# Revit family: 01-70-035-DN40-80
name_source: partatom
category: Pipe Accessories
units: mm (PartAtom-declared; Revit-internal decimal feet)

## family parameters
Always vertical = No
Cut with Voids When Loaded = No
Part Type = Valve - Breaks Into
Round Connector Dimension = Use Diameter
Shared = No
Work Plane-Based = No

## types (4) — shared parameters
Body_Wallthickness = 10 mm  [stored 0.0328084 ft]
Body_Wallthickness_1 = 20 mm  [stored 0.0656168 ft]
Body_Wallthickness_2 = 5 mm  [stored 0.0164042 ft]
Bonnet_Flange_cut = 8 mm  [stored 0.0262467 ft]
Bonnet_Flange_thickness = 15 mm  [stored 0.0492126 ft]
D = 63 mm
D1 = 10 mm  [stored 0.0328084 ft]
DN040_PN16 = 01-050-70-016
DN050_PN16 = 01-063-70-016
DN065_PN16 = 01-075-70-016
DN080_PN16 = 01-090-70-0146499
Description_ = AVK GATE VALVE, SUPA PLUS™
Fillet_Thickness = 6 mm  [stored 0.019685 ft]
Flange_Thickness = 19 mm  [stored 0.062336 ft]
Flange_width = 30 mm  [stored 0.0984252 ft]
Ftc = 4 mm  [stored 0.0131234 ft]
L1 = 229 mm
Name_Height_reference = 10 mm  [stored 0.0328084 ft]
R2f = 15 mm  [stored 0.0492126 ft]
Rib_Height_Reference_1 = 120 mm
Rib_Height_Reference_2 = 110 mm
Rib_Height_Reference_3 = 100 mm
Rib_Thickness = 18 mm  [stored 0.0590551 ft]
Search_table = 01-70-035-DN40-80
URL product pages = https://www.avkvalves.com
zero-valued in all types: Bottom_Reference

## per-type parameters (varying)
- DN040_PN16: At=46 mm  [stored 0.150919 ft]; Body_Height=101 mm; Body_depth=92 mm; Body_width=74 mm; Bonnet_Flange_Depth=118 mm; Bonnet_Flange_Width=68 mm; Bonnet_Height=38 mm; Bonnet_Reference_height=91 mm; Bonnet_Thickness=75 mm; Bt=75 mm; Bt_2=68 mm; CL _Thickness=26 mm; CL_Height=51 mm; Cut_Reference=624 mm; D2=29 mm  [stored 0.0951444 ft]; Dd=50 mm; Dd_ref=45 mm  [stored 0.147638 ft]; Dd_ref_1=25 mm  [stored 0.082021 ft]; E=14 mm  [stored 0.0459318 ft]; F=7 mm  [stored 0.0229659 ft]; F1=17 mm  [stored 0.0557743 ft]; Flange_OR=75 mm; Flange_Thickness_cut=28 mm; Flange_depth=154 mm; Ftc_reference_height=75 mm; H=236 mm; H1=207 mm; H2=44 mm  [stored 0.144357 ft]; H3=280 mm; Horizontal_Flange_width=88 mm; ID (Radius)=20 mm  [stored 0.0656168 ft]; L=312 mm; L2=64 mm; L_Dia=40 mm  [stored 0.131234 ft]; L_ref=271 mm; Name_Reference=67 mm; Name_Width=37 mm  [stored 0.121391 ft]; Neck_H=56 mm; Neck_T=24 mm  [stored 0.0787402 ft]; Neck_T2=22 mm  [stored 0.0721785 ft]; Nominal Diameter (DN)=40 mm  [stored 0.131234 ft]; OD=39 mm  [stored 0.127953 ft]; R1tv=750 mm; RF_Dia=42 mm  [stored 0.137795 ft]; Rf=147 mm; Rib_Height_Reference_4=40 mm  [stored 0.131234 ft]; Rib_Width_1=37 mm  [stored 0.121391 ft]; Rib_Width_2=37 mm  [stored 0.121391 ft]; Rib_Width_3=37 mm  [stored 0.121391 ft]; Rib_depth_1=37 mm  [stored 0.121391 ft]; Rib_depth_2=37 mm  [stored 0.121391 ft]; Rib_depth_3=37 mm  [stored 0.121391 ft]; Rt=250 mm
- DN050_PN16: At=50 mm; Body_Height=101 mm; Body_depth=100 mm; Body_width=72 mm; Bonnet_Flange_Depth=118 mm; Bonnet_Flange_Width=82 mm; Bonnet_Height=41 mm; Bonnet_Reference_height=91 mm; Bonnet_Thickness=73 mm; Bt=73 mm; Bt_2=66 mm; CL _Thickness=25 mm  [stored 0.082021 ft]; CL_Height=55 mm; Cut_Reference=624 mm; D2=29 mm  [stored 0.0951444 ft]; Dd=63 mm; Dd_ref=52 mm; Dd_ref_1=32 mm  [stored 0.104987 ft]; E=11 mm  [stored 0.0360892 ft]; F=7 mm  [stored 0.0229659 ft]; F1=17 mm  [stored 0.0557743 ft]; Flange_OR=83 mm; Flange_Thickness_cut=29 mm  [stored 0.0951444 ft]; Flange_depth=169 mm; Ftc_reference_height=83 mm; H=241 mm; H1=212 mm; H2=52 mm; H3=293 mm; Horizontal_Flange_width=104 mm; ID (Radius)=25 mm  [stored 0.082021 ft]; L=312 mm; L2=68 mm; L_Dia=50 mm; L_ref=271 mm; Name_Reference=71 mm; Name_Width=36 mm  [stored 0.11811 ft]; Neck_H=57 mm; Neck_T=23 mm  [stored 0.0754593 ft]; Neck_T2=21 mm  [stored 0.0688976 ft]; Nominal Diameter (DN)=50 mm; OD=43 mm; R1tv=825 mm; RF_Dia=50 mm; Rf=173 mm; Rib_Height_Reference_4=60 mm; Rib_Width_1=36 mm  [stored 0.11811 ft]; Rib_Width_2=36 mm  [stored 0.11811 ft]; Rib_Width_3=36 mm  [stored 0.11811 ft]; Rib_depth_1=36 mm  [stored 0.11811 ft]; Rib_depth_2=36 mm  [stored 0.11811 ft]; Rib_depth_3=36 mm  [stored 0.11811 ft]; Rt=275 mm
- DN065_PN16: At=60 mm; Body_Height=115 mm; Body_depth=120 mm; Body_width=72 mm; Bonnet_Flange_Depth=135 mm; Bonnet_Flange_Width=65 mm; Bonnet_Height=47 mm; Bonnet_Reference_height=105 mm; Bonnet_Thickness=73 mm; Bt=73 mm; Bt_2=66 mm; CL _Thickness=25 mm  [stored 0.082021 ft]; CL_Height=65 mm; Cut_Reference=624 mm; D2=34 mm  [stored 0.111549 ft]; Dd=75 mm; Dd_ref=58 mm; Dd_ref_1=38 mm; E=11 mm  [stored 0.0360892 ft]; F=9 mm; F1=20 mm  [stored 0.0656168 ft]; Flange_OR=93 mm; Flange_Thickness_cut=30 mm  [stored 0.0984252 ft]; Flange_depth=179 mm; Ftc_reference_height=93 mm; H=271 mm; H1=237 mm; H2=58 mm; H3=329 mm; Horizontal_Flange_width=116 mm; ID (Radius)=33 mm; L=312 mm; L2=70 mm; L_Dia=65 mm; L_ref=271 mm; Name_Reference=96 mm; Name_Width=36 mm  [stored 0.11811 ft]; Neck_H=57 mm; Neck_T=23 mm  [stored 0.0754593 ft]; Neck_T2=21 mm  [stored 0.0688976 ft]; Nominal Diameter (DN)=65 mm; OD=49 mm; R1tv=930 mm; RF_Dia=59 mm; Rf=193 mm; Rib_Height_Reference_4=75 mm; Rib_Width_1=36 mm  [stored 0.11811 ft]; Rib_Width_2=36 mm  [stored 0.11811 ft]; Rib_Width_3=36 mm  [stored 0.11811 ft]; Rib_depth_1=36 mm  [stored 0.11811 ft]; Rib_depth_2=36 mm  [stored 0.11811 ft]; Rib_depth_3=36 mm  [stored 0.11811 ft]; Rt=310 mm
- DN080_PN16: At=70 mm; Body_Height=108 mm; Body_depth=140 mm; Body_width=75 mm; Bonnet_Flange_Depth=171 mm; Bonnet_Flange_Width=76 mm; Bonnet_Height=50 mm; Bonnet_Reference_height=98 mm; Bonnet_Thickness=77 mm; Bt=77 mm; Bt_2=69 mm; CL _Thickness=27 mm  [stored 0.0885827 ft]; CL_Height=75 mm; Cut_Reference=660 mm; D2=34 mm  [stored 0.111549 ft]; Dd=90 mm; Dd_ref=65 mm; Dd_ref_1=45 mm  [stored 0.147638 ft]; E=15 mm  [stored 0.0492126 ft]; F=9 mm; F1=20 mm  [stored 0.0656168 ft]; Flange_OR=100 mm; Flange_Thickness_cut=30 mm  [stored 0.0984252 ft]; Flange_depth=199 mm; Ftc_reference_height=100 mm; H=282 mm; H1=248 mm; H2=66 mm; H3=348 mm; Horizontal_Flange_width=132 mm; ID (Radius)=40 mm  [stored 0.131234 ft]; L=330 mm; L2=66 mm; L_Dia=80 mm; L_ref=280 mm; Name_Reference=90 mm; Name_Width=38 mm; Neck_H=65 mm; Neck_T=25 mm  [stored 0.082021 ft]; Neck_T2=23 mm  [stored 0.0754593 ft]; Nominal Diameter (DN)=80 mm; OD=56 mm; R1tv=1000 mm; RF_Dia=66 mm; Rf=220 mm; Rib_Height_Reference_4=85 mm; Rib_Width_1=38 mm; Rib_Width_2=38 mm; Rib_Width_3=38 mm; Rib_depth_1=38 mm; Rib_depth_2=38 mm; Rib_depth_3=38 mm; Rt=333 mm

note: [stored X ft] marks values corroborated as IEEE doubles in the binary element streams (Revit-internal decimal feet)

## geometry (parser evidence)
native form markers: Sweep x2
no freeform markers — native parametric forms only
